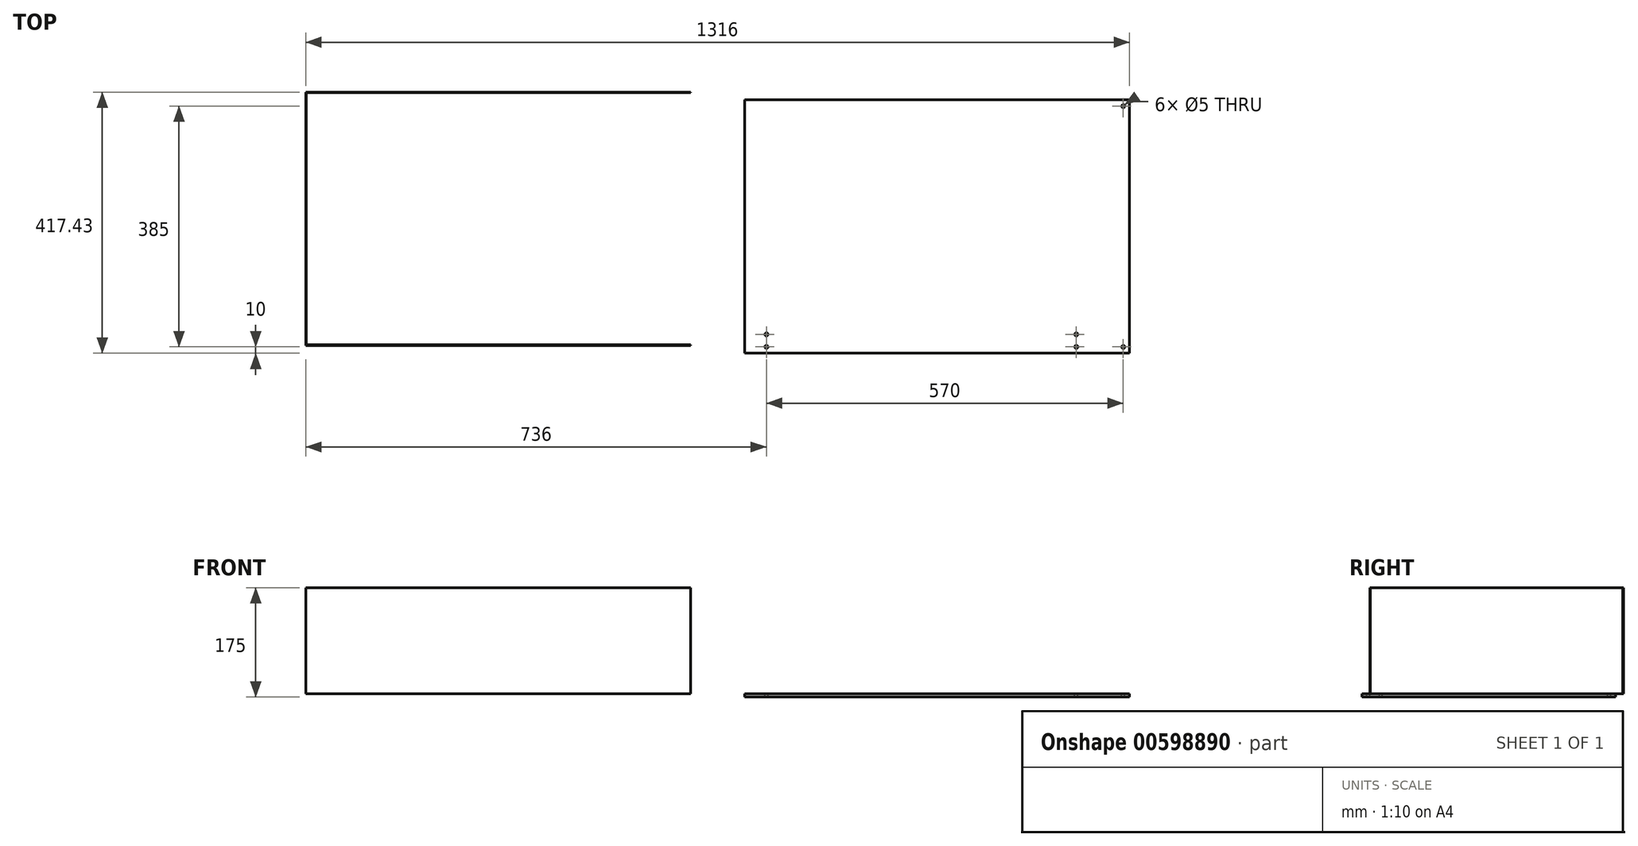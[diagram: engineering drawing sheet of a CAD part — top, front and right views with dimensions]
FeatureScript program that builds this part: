
annotation { "Feature Type Name" : "Feature", "Feature Type Description" : "" }
export const myFeature = defineFeature(function(context is Context, id is Id, definition is map)
    precondition{}
    {
        {
            var Q0;
            Q0=qCreatedBy(makeId("Top.planeOp"),FACE);
            var sketch = newSketch(context, id + "F0", { "sketchPlane" : qUnion([Q0])});
            skLineSegment(sketch, "E0.bottom", {"start": v(307.5, -202.5) * mm, "end": v(-307.5, -202.5) * mm});
            skLineSegment(sketch, "E0.top", {"start": v(307.5, 202.5) * mm, "end": v(-307.5, 202.5) * mm});
            skLineSegment(sketch, "E0.left", {"start": v(307.5, -202.5) * mm, "end": v(307.5, 202.5) * mm});
            skLineSegment(sketch, "E0.right", {"start": v(-307.5, -202.5) * mm, "end": v(-307.5, 202.5) * mm});
            skPoint(sketch, "E0.middle", {"position": v(0, 0) * mm});
            skSolve(sketch);
        }
        {
            var Q0;
            Q0=makeQuery(id+"F0.imprint","IMPRINT",FACE,{"disambiguationData":[TD([[makeQuery(id+"F0.imprint","IMPRINT",EDGE,{"derivedFrom":sQuery(id+"F0.wireOp",EDGE,"E0.bottom")}),-1.0]])]});
            extrude(context, id + "F1", {"entities" : qUnion([Q0]), "depth" : 5 * mm, "offsetDistance" : 25 * mm});
        }
        {
            var Q0;
            Q0=makeQuery(id+"F1.opExtrude","CAP_FACE",FACE,{"disambiguationData":[OSD([sQuery(id+"F0.wireOp",EDGE,"E0.bottom"),sQuery(id+"F0.wireOp",EDGE,"E0.top"),sQuery(id+"F0.wireOp",EDGE,"E0.left"),sQuery(id+"F0.wireOp",EDGE,"E0.right")])],"isStart":false});
            var sketch = newSketch(context, id + "F2", { "sketchPlane" : qUnion([Q0])});
            skLineSegment(sketch, "E1", {"start": v(-307.5, 201.5) * mm, "end": v(306.5, 201.5) * mm});
            skLineSegment(sketch, "E2", {"start": v(306.5, 201.5) * mm, "end": v(306.5, -201.5) * mm});
            skLineSegment(sketch, "E3", {"start": v(306.5, -201.5) * mm, "end": v(-307.5, -201.5) * mm});
            skLineSegment(sketch, "E4", {"start": v(-307.5, -201.5) * mm, "end": v(-307.5, -202.5) * mm});
            skLineSegment(sketch, "E5", {"start": v(-307.5, -202.5) * mm, "end": v(307.5, -202.5) * mm});
            skLineSegment(sketch, "E6", {"start": v(307.5, -202.5) * mm, "end": v(307.5, 202.5) * mm});
            skLineSegment(sketch, "E7", {"start": v(307.5, 202.5) * mm, "end": v(-307.5, 202.5) * mm});
            skLineSegment(sketch, "E8", {"start": v(-307.5, 202.5) * mm, "end": v(-307.5, 201.5) * mm});
            skSolve(sketch);
        }
        {
            var Q0;
            {var subQ0=sQuery(id+"F2.wireOp",EDGE,"E1");Q0=makeQuery(id+"F2.imprint","IMPRINT",FACE,{"disambiguationData":[TD([[makeQuery(id+"F2.imprint","IMPRINT",EDGE,{"derivedFrom":subQ0}),-1.0]])]});}
            var sketch = newSketch(context, id + "F3", { "sketchPlane" : qUnion([Q0])});
            skLineSegment(sketch, "E9", {"start": v(-393.5, -190.07) * mm, "end": v(-1008.5, -190.07) * mm});
            skLineSegment(sketch, "E10", {"start": v(-1008.5, -190.07) * mm, "end": v(-1008.5, 214.93) * mm});
            skLineSegment(sketch, "E11", {"start": v(-1008.5, 214.93) * mm, "end": v(-393.5, 214.93) * mm});
            skLineSegment(sketch, "E12", {"start": v(-393.5, 214.93) * mm, "end": v(-393.5, 213.93) * mm});
            skLineSegment(sketch, "E13", {"start": v(-393.5, 213.93) * mm, "end": v(-1007.5, 213.93) * mm});
            skLineSegment(sketch, "E14", {"start": v(-1007.5, 213.93) * mm, "end": v(-1007.5, -189.07) * mm});
            skLineSegment(sketch, "E15", {"start": v(-1007.5, -189.07) * mm, "end": v(-393.5, -189.07) * mm});
            skLineSegment(sketch, "E16", {"start": v(-393.5, -189.07) * mm, "end": v(-393.5, -190.07) * mm});
            skSolve(sketch);
        }
        {
            var Q0;
            Q0=qSketchRegion(id+"F3",true);
            extrude(context, id + "F4", {"entities" : qUnion([Q0]), "depth" : 170 * mm, "offsetDistance" : 25 * mm});
        }
        {
            var Q0;
            Q0=makeQuery(id+"F1.opExtrude","CAP_FACE",FACE,{"disambiguationData":[OSD([sQuery(id+"F0.wireOp",EDGE,"E0.bottom"),sQuery(id+"F0.wireOp",EDGE,"E0.top"),sQuery(id+"F0.wireOp",EDGE,"E0.left"),sQuery(id+"F0.wireOp",EDGE,"E0.right")])],"isStart":true});
            var sketch = newSketch(context, id + "F5", { "sketchPlane" : qUnion([Q0])});
            skLineSegment(sketch, "E17", {"start": v(-272.5, 202.5) * mm, "end": v(-272.5, 173.6) * mm});
            skPoint(sketch, "E18", {"position": v(-272.5, 192.5) * mm});
            skSolve(sketch);
        }
        {
            var Q0;
            Q0=sQuery(id+"F5.wireOp",VERTEX,"E18");
            var Q1;
            Q1=makeQuery(id+"F1.opExtrude","SWEPT_BODY",BODY,{"disambiguationData":[OSD([sQuery(id+"F0.wireOp",EDGE,"E0.bottom"),sQuery(id+"F0.wireOp",EDGE,"E0.top"),sQuery(id+"F0.wireOp",EDGE,"E0.left"),sQuery(id+"F0.wireOp",EDGE,"E0.right")])]});
            hole(context, id + "F6", {"style" : HoleStyle.SIMPLE, "endStyle" : HoleEndStyle.THROUGH, "holeDiameter" : 5 * mm, "majorDiameter" : 5 * mm, "isTappedThrough" : true, "tappedDepth" : 12 * mm, "tapClearance" : 3, "locations" : qUnion([Q0]), "scope" : qUnion([Q1])});
        }
        {
            var Q0;
            Q0=makeQuery(id+"F1.opExtrude","CAP_FACE",FACE,{"disambiguationData":[OSD([sQuery(id+"F0.wireOp",EDGE,"E0.bottom"),sQuery(id+"F0.wireOp",EDGE,"E0.top"),sQuery(id+"F0.wireOp",EDGE,"E0.left"),sQuery(id+"F0.wireOp",EDGE,"E0.right")])],"isStart":true});
            var sketch = newSketch(context, id + "F7", { "sketchPlane" : qUnion([Q0])});
            skLineSegment(sketch, "E19", {"start": v(-272.5, 202.5) * mm, "end": v(-272.5, 172.5) * mm});
            skSolve(sketch);
        }
        {
            var Q0;
            Q0=sQuery(id+"F7.wireOp",VERTEX,"E19.end");
            var Q1;
            Q1=makeQuery(id+"F1.opExtrude","SWEPT_BODY",BODY,{"disambiguationData":[OSD([sQuery(id+"F0.wireOp",EDGE,"E0.bottom"),sQuery(id+"F0.wireOp",EDGE,"E0.top"),sQuery(id+"F0.wireOp",EDGE,"E0.left"),sQuery(id+"F0.wireOp",EDGE,"E0.right")])]});
            hole(context, id + "F8", {"style" : HoleStyle.SIMPLE, "endStyle" : HoleEndStyle.THROUGH, "holeDiameter" : 5 * mm, "majorDiameter" : 5 * mm, "isTappedThrough" : true, "tappedDepth" : 12 * mm, "tapClearance" : 3, "locations" : qUnion([Q0]), "scope" : qUnion([Q1])});
        }
        {
            var Q0;
            Q0=makeQuery(id+"F1.opExtrude","CAP_FACE",FACE,{"disambiguationData":[OSD([sQuery(id+"F0.wireOp",EDGE,"E0.bottom"),sQuery(id+"F0.wireOp",EDGE,"E0.top"),sQuery(id+"F0.wireOp",EDGE,"E0.left"),sQuery(id+"F0.wireOp",EDGE,"E0.right")])],"isStart":true});
            var sketch = newSketch(context, id + "F9", { "sketchPlane" : qUnion([Q0])});
            skLineSegment(sketch, "E20", {"start": v(222.5, 202.5) * mm, "end": v(222.5, 192.5) * mm});
            skSolve(sketch);
        }
        {
            var Q0;
            Q0=sQuery(id+"F9.wireOp",VERTEX,"E20.end");
            var Q1;
            Q1=makeQuery(id+"F1.opExtrude","SWEPT_BODY",BODY,{"disambiguationData":[OSD([sQuery(id+"F0.wireOp",EDGE,"E0.bottom"),sQuery(id+"F0.wireOp",EDGE,"E0.top"),sQuery(id+"F0.wireOp",EDGE,"E0.left"),sQuery(id+"F0.wireOp",EDGE,"E0.right")])]});
            hole(context, id + "F10", {"style" : HoleStyle.SIMPLE, "endStyle" : HoleEndStyle.THROUGH, "holeDiameter" : 5 * mm, "majorDiameter" : 5 * mm, "isTappedThrough" : true, "tappedDepth" : 12 * mm, "tapClearance" : 3, "locations" : qUnion([Q0]), "scope" : qUnion([Q1])});
        }
        {
            var Q0;
            Q0=makeQuery(id+"F1.opExtrude","CAP_FACE",FACE,{"disambiguationData":[OSD([sQuery(id+"F0.wireOp",EDGE,"E0.bottom"),sQuery(id+"F0.wireOp",EDGE,"E0.top"),sQuery(id+"F0.wireOp",EDGE,"E0.left"),sQuery(id+"F0.wireOp",EDGE,"E0.right")])],"isStart":true});
            var sketch = newSketch(context, id + "F11", { "sketchPlane" : qUnion([Q0])});
            skLineSegment(sketch, "E21", {"start": v(222.5, 202.5) * mm, "end": v(222.5, 172.5) * mm});
            skSolve(sketch);
        }
        {
            var Q0;
            Q0=sQuery(id+"F11.wireOp",VERTEX,"E21.end");
            var Q1;
            Q1=makeQuery(id+"F1.opExtrude","SWEPT_BODY",BODY,{"disambiguationData":[OSD([sQuery(id+"F0.wireOp",EDGE,"E0.bottom"),sQuery(id+"F0.wireOp",EDGE,"E0.top"),sQuery(id+"F0.wireOp",EDGE,"E0.left"),sQuery(id+"F0.wireOp",EDGE,"E0.right")])]});
            hole(context, id + "F12", {"style" : HoleStyle.SIMPLE, "endStyle" : HoleEndStyle.THROUGH, "holeDiameter" : 5 * mm, "majorDiameter" : 5 * mm, "isTappedThrough" : true, "tappedDepth" : 12 * mm, "tapClearance" : 3, "locations" : qUnion([Q0]), "scope" : qUnion([Q1])});
        }
        {
            var Q0;
            Q0=makeQuery(id+"F1.opExtrude","CAP_FACE",FACE,{"disambiguationData":[OSD([sQuery(id+"F0.wireOp",EDGE,"E0.bottom"),sQuery(id+"F0.wireOp",EDGE,"E0.top"),sQuery(id+"F0.wireOp",EDGE,"E0.left"),sQuery(id+"F0.wireOp",EDGE,"E0.right")])],"isStart":true});
            var sketch = newSketch(context, id + "F13", { "sketchPlane" : qUnion([Q0])});
            skLineSegment(sketch, "E22", {"start": v(297.5, -202.5) * mm, "end": v(297.5, -192.5) * mm});
            skSolve(sketch);
        }
        {
            var Q0;
            Q0=sQuery(id+"F13.wireOp",VERTEX,"E22.end");
            var Q1;
            Q1=makeQuery(id+"F1.opExtrude","SWEPT_BODY",BODY,{"disambiguationData":[OSD([sQuery(id+"F0.wireOp",EDGE,"E0.bottom"),sQuery(id+"F0.wireOp",EDGE,"E0.top"),sQuery(id+"F0.wireOp",EDGE,"E0.left"),sQuery(id+"F0.wireOp",EDGE,"E0.right")])]});
            hole(context, id + "F14", {"style" : HoleStyle.SIMPLE, "endStyle" : HoleEndStyle.THROUGH, "holeDiameter" : 5 * mm, "majorDiameter" : 5 * mm, "isTappedThrough" : true, "tappedDepth" : 12 * mm, "tapClearance" : 3, "locations" : qUnion([Q0]), "scope" : qUnion([Q1])});
        }
        {
            var Q0;
            Q0=makeQuery(id+"F1.opExtrude","CAP_FACE",FACE,{"disambiguationData":[OSD([sQuery(id+"F0.wireOp",EDGE,"E0.bottom"),sQuery(id+"F0.wireOp",EDGE,"E0.top"),sQuery(id+"F0.wireOp",EDGE,"E0.left"),sQuery(id+"F0.wireOp",EDGE,"E0.right")])],"isStart":true});
            var sketch = newSketch(context, id + "F15", { "sketchPlane" : qUnion([Q0])});
            skLineSegment(sketch, "E23", {"start": v(297.5, 202.5) * mm, "end": v(297.5, 192.5) * mm});
            skSolve(sketch);
        }
        {
            var Q0;
            Q0=sQuery(id+"F15.wireOp",VERTEX,"E23.end");
            var Q1;
            Q1=makeQuery(id+"F1.opExtrude","SWEPT_BODY",BODY,{"disambiguationData":[OSD([sQuery(id+"F0.wireOp",EDGE,"E0.bottom"),sQuery(id+"F0.wireOp",EDGE,"E0.top"),sQuery(id+"F0.wireOp",EDGE,"E0.left"),sQuery(id+"F0.wireOp",EDGE,"E0.right")])]});
            hole(context, id + "F16", {"style" : HoleStyle.SIMPLE, "endStyle" : HoleEndStyle.THROUGH, "holeDiameter" : 5 * mm, "majorDiameter" : 5 * mm, "isTappedThrough" : true, "tappedDepth" : 12 * mm, "tapClearance" : 3, "locations" : qUnion([Q0]), "scope" : qUnion([Q1])});
        }
    });
